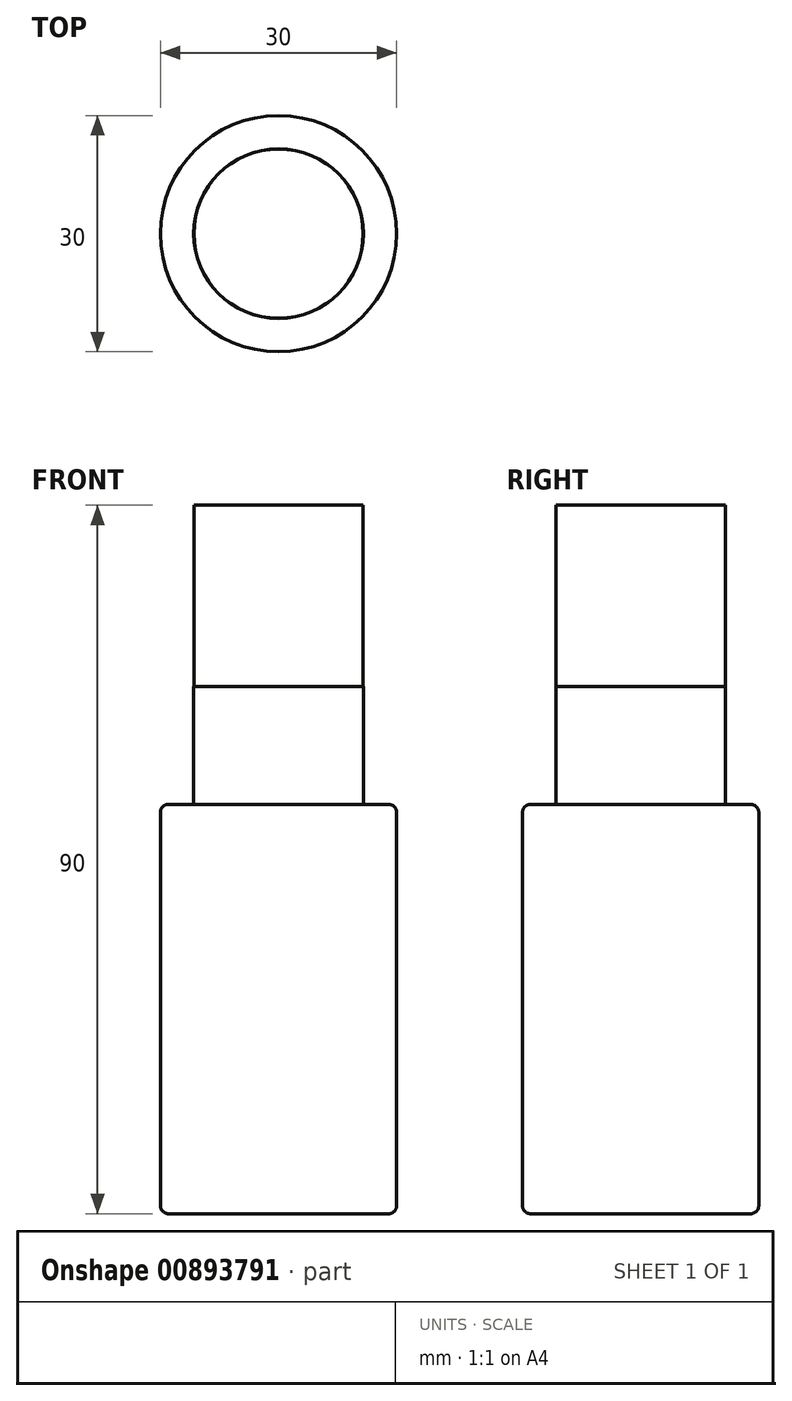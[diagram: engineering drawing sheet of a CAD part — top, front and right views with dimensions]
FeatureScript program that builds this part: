
annotation { "Feature Type Name" : "Feature", "Feature Type Description" : "" }
export const myFeature = defineFeature(function(context is Context, id is Id, definition is map)
    precondition{}
    {
        {
            var Q0;
            Q0=qCreatedBy(makeId("Front.planeOp"),FACE);
            var sketch = newSketch(context, id + "F0", { "sketchPlane" : qUnion([Q0])});
            skLineSegment(sketch, "E0", {"start": v(0, 49.8) * mm, "end": v(10.75, 49.8) * mm});
            skLineSegment(sketch, "E1", {"start": v(10.75, 49.8) * mm, "end": v(10.75, 26.8) * mm});
            skLineSegment(sketch, "E2", {"start": v(10.75, 26.8) * mm, "end": v(10.78, 26.8) * mm});
            skLineSegment(sketch, "E3", {"start": v(10.77, 26.8) * mm, "end": v(10.78, 11.8) * mm});
            skLineSegment(sketch, "E4", {"start": v(0, 11.8) * mm, "end": v(0, 49.8) * mm});
            skPoint(sketch, "E5.end.orphan", {"position": v(0, 26.8) * mm});
            skLineSegment(sketch, "E6", {"start": v(10.78, 11.8) * mm, "end": v(15, 11.8) * mm});
            skLineSegment(sketch, "E7", {"start": v(15, 11.8) * mm, "end": v(15, -40.2) * mm});
            skLineSegment(sketch, "E8", {"start": v(15, -40.2) * mm, "end": v(0, -40.2) * mm});
            skLineSegment(sketch, "E9", {"start": v(0, 11.8) * mm, "end": v(0, -40.2) * mm});
            skSolve(sketch);
        }
        {
            var Q0;
            Q0=makeQuery(id+"F0.imprint","IMPRINT",FACE,{"disambiguationData":[TD([[makeQuery(id+"F0.imprint","IMPRINT",EDGE,{"derivedFrom":sQuery(id+"F0.wireOp",EDGE,"E0")}),-1.0]])]});
            var Q1;
            Q1=sQuery(id+"F0.wireOp",EDGE,"E4");
            revolve(context, id + "F1", {"surfaceOperationType" : NewSurfaceOperationType.NEW, "entities" : qUnion([Q0]), "axis" : qUnion([Q1]), "revolveType" : RevolveType.FULL});
        }
        {
            var Q0;
            Q0=makeQuery(id+"F1.opRevolve","SWEPT_EDGE",EDGE,{"disambiguationData":[OSD([sQuery(id+"F0.wireOp",EDGE,"E6"),sQuery(id+"F0.wireOp",EDGE,"E7")])]});
            fillet(context, id + "F2", {"entities" : qUnion([Q0]), "radius" : 1 * mm, "tangentPropagation" : true, "allowEdgeOverflow" : false});
        }
        {
            var Q0;
            Q0=makeQuery(id+"F1.opRevolve","SWEPT_EDGE",EDGE,{"disambiguationData":[OSD([sQuery(id+"F0.wireOp",EDGE,"E7"),sQuery(id+"F0.wireOp",EDGE,"E8")])]});
            fillet(context, id + "F3", {"entities" : qUnion([Q0]), "radius" : 1 * mm, "tangentPropagation" : true, "allowEdgeOverflow" : false});
        }
    });
